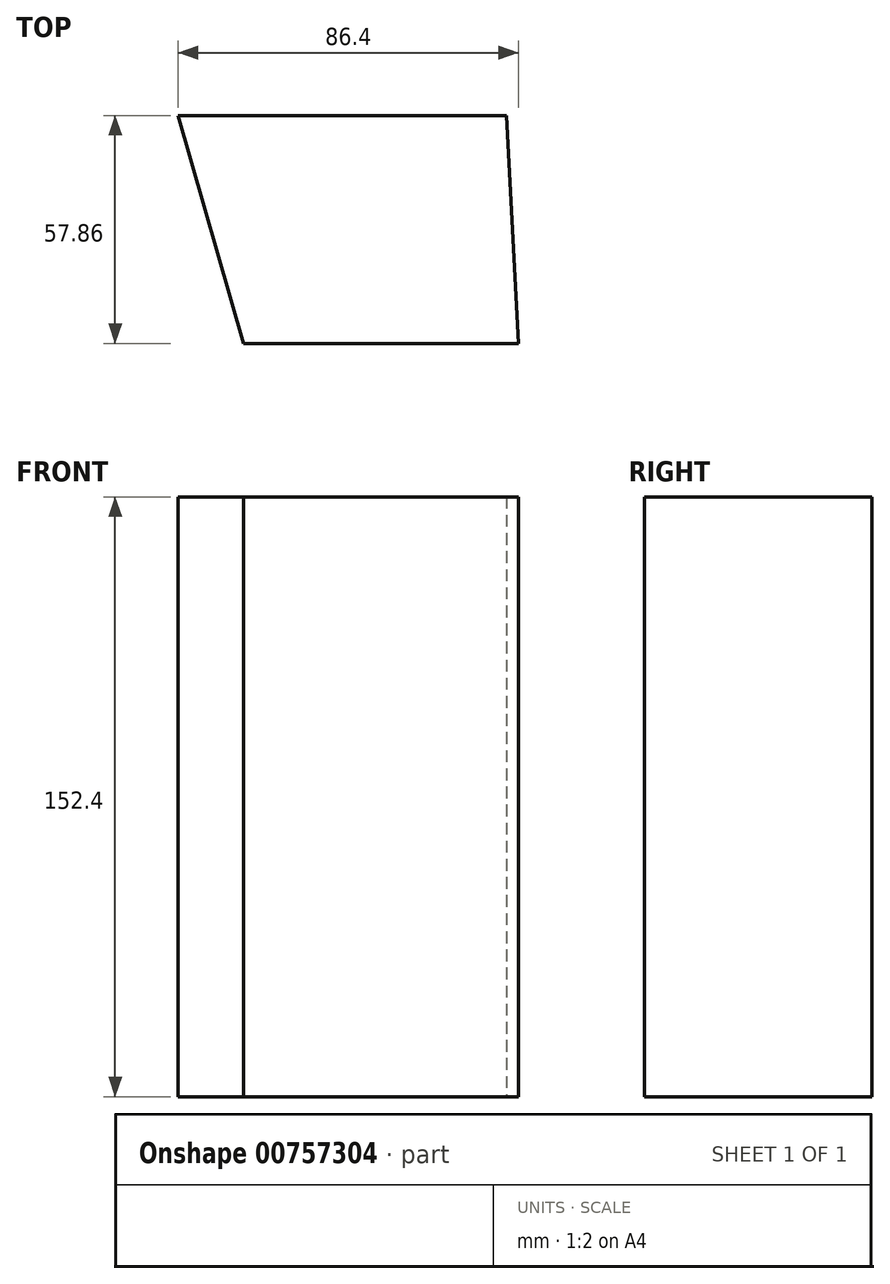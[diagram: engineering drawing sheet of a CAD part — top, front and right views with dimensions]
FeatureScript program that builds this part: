
annotation { "Feature Type Name" : "Feature", "Feature Type Description" : "" }
export const myFeature = defineFeature(function(context is Context, id is Id, definition is map)
    precondition{}
    {
        {
            var Q0;
            Q0=qCreatedBy(makeId("Top.planeOp"),FACE);
            var sketch = newSketch(context, id + "F0", { "sketchPlane" : qUnion([Q0])});
            skLineSegment(sketch, "E0", {"start": v(-38.4, 38.8) * mm, "end": v(45, 38.8) * mm});
            skLineSegment(sketch, "E1", {"start": v(45, 38.8) * mm, "end": v(47.99, -19.05) * mm});
            skLineSegment(sketch, "E2", {"start": v(47.99, -19.05) * mm, "end": v(-21.85, -19.05) * mm});
            skLineSegment(sketch, "E3", {"start": v(-21.85, -19.05) * mm, "end": v(-38.4, 38.8) * mm});
            skCircle(sketch, "E4", {"center": v(0, 0) * mm, "radius": 15.64 * mm});
            skSolve(sketch);
        }
        {
            var Q0;
            Q0 = qSketchRegion(id + "F0", true);
            var Q1;
            Q1=makeQuery(id+"F0.imprint","IMPRINT",FACE,{"disambiguationData":[TD([[makeQuery(id+"F0.imprint","IMPRINT",EDGE,{"derivedFrom":sQuery(id+"F0.wireOp",EDGE,"E4")}),1.0]])]});
            extrude(context, id + "F1", {"entities" : qUnion([Q0, Q1]), "depth" : 152.4 * mm, "offsetDistance" : 25.4 * mm});
        }
    });
